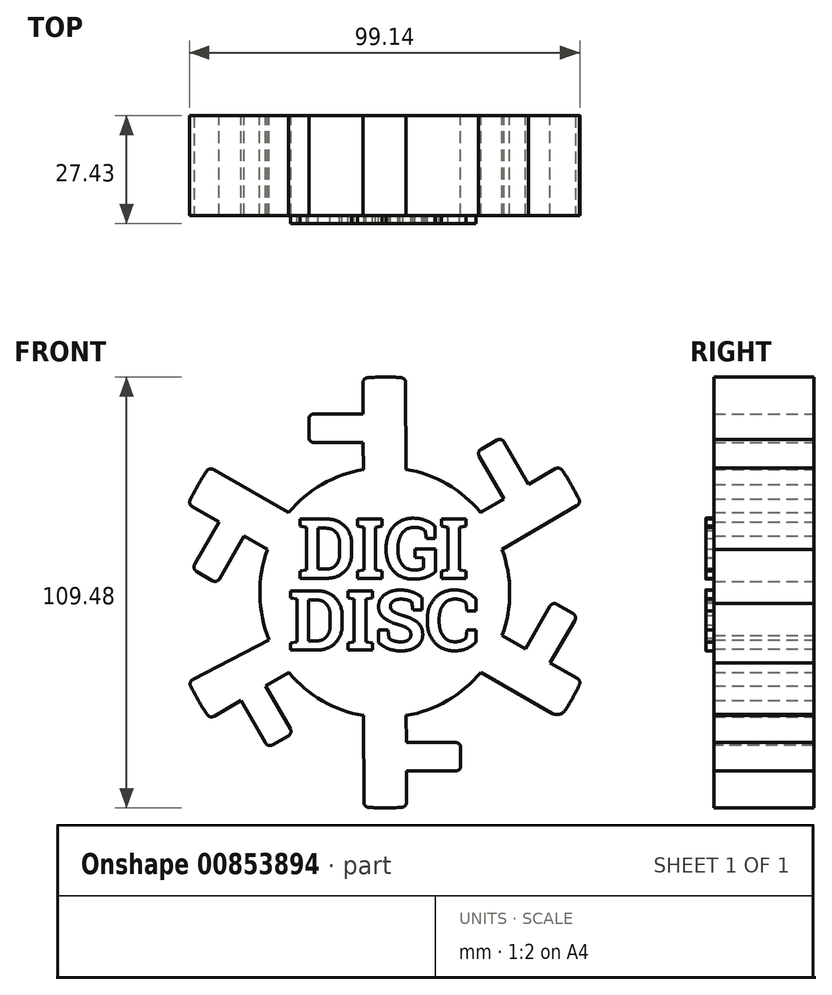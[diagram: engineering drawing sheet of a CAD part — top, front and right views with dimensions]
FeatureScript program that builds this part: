
annotation { "Feature Type Name" : "Feature", "Feature Type Description" : "" }
export const myFeature = defineFeature(function(context is Context, id is Id, definition is map)
    precondition{}
    {
        {
            var Q0;
            Q0=qCreatedBy(makeId("Front.planeOp"),FACE);
            var sketch = newSketch(context, id + "F0", { "sketchPlane" : qUnion([Q0])});
            skArc(sketch, "E0", {"start": v(5.31, 54.48) * mm, "mid": v(-0.12, 54.74) * mm, "end": v(-5.54, 54.46) * mm});
            skCircle(sketch, "E1", {"center": v(0, 0) * mm, "radius": 31.75 * mm});
            skLineSegment(sketch, "E2.left", {"start": v(-5.45, 31.28) * mm, "end": v(-5.48, 38.1) * mm});
            skLineSegment(sketch, "E2.right", {"start": v(5.4, 31.29) * mm, "end": v(5.31, 54.48) * mm});
            skLineSegment(sketch, "E3.bottom", {"start": v(-5.48, 38.1) * mm, "end": v(-19.28, 38.1) * mm});
            skLineSegment(sketch, "E3.top", {"start": v(-5.5, 45.36) * mm, "end": v(-19.28, 45.36) * mm});
            skLineSegment(sketch, "E3.left", {"start": v(5.38, 38.1) * mm, "end": v(5.38, 45.36) * mm});
            skLineSegment(sketch, "E3.right", {"start": v(-19.28, 38.1) * mm, "end": v(-19.28, 45.36) * mm});
            skLineSegment(sketch, "E4.trimOffspring", {"start": v(-5.5, 45.36) * mm, "end": v(-5.54, 54.46) * mm});
            skLineSegment(sketch, "E5.1.0", {"start": v(-30.3, 23.7) * mm, "end": v(-36.6, 27.34) * mm});
            skLineSegment(sketch, "E5.1.1", {"start": v(-24.4, 20.32) * mm, "end": v(-44.53, 31.84) * mm});
            skArc(sketch, "E5.1.2", {"start": v(-44.53, 31.84) * mm, "mid": v(-47.47, 27.27) * mm, "end": v(-49.94, 22.43) * mm});
            skLineSegment(sketch, "E5.1.3", {"start": v(-42.04, 17.9) * mm, "end": v(-49.94, 22.43) * mm});
            skLineSegment(sketch, "E5.1.4", {"start": v(-29.81, 10.92) * mm, "end": v(-35.74, 14.3) * mm});
            skLineSegment(sketch, "E5.1.5", {"start": v(-35.74, 14.3) * mm, "end": v(-42.64, 2.35) * mm});
            skLineSegment(sketch, "E5.1.6", {"start": v(-42.64, 2.35) * mm, "end": v(-48.92, 5.98) * mm});
            skLineSegment(sketch, "E5.1.7", {"start": v(-42.04, 17.9) * mm, "end": v(-48.92, 5.98) * mm});
            skArc(sketch, "E5.2.2", {"start": v(-49.84, -22.64) * mm, "mid": v(-47.35, -27.47) * mm, "end": v(-44.4, -32.03) * mm});
            skLineSegment(sketch, "E5.2.3", {"start": v(-36.53, -27.45) * mm, "end": v(-44.4, -32.03) * mm});
            skLineSegment(sketch, "E5.2.4", {"start": v(-24.36, -20.36) * mm, "end": v(-30.26, -23.8) * mm});
            skLineSegment(sketch, "E5.2.5", {"start": v(-30.26, -23.8) * mm, "end": v(-23.35, -35.75) * mm});
            skLineSegment(sketch, "E5.2.6", {"start": v(-23.35, -35.75) * mm, "end": v(-29.64, -39.38) * mm});
            skLineSegment(sketch, "E5.2.7", {"start": v(-36.53, -27.45) * mm, "end": v(-29.64, -39.38) * mm});
            skLineSegment(sketch, "E5.3.1", {"start": v(-5.4, -31.29) * mm, "end": v(-5.31, -54.48) * mm});
            skArc(sketch, "E5.3.2", {"start": v(-5.31, -54.48) * mm, "mid": v(0.12, -54.74) * mm, "end": v(5.54, -54.46) * mm});
            skLineSegment(sketch, "E5.3.3", {"start": v(5.5, -45.36) * mm, "end": v(5.54, -54.46) * mm});
            skLineSegment(sketch, "E5.3.4", {"start": v(5.45, -31.28) * mm, "end": v(5.48, -38.1) * mm});
            skLineSegment(sketch, "E5.3.5", {"start": v(5.48, -38.1) * mm, "end": v(19.28, -38.1) * mm});
            skLineSegment(sketch, "E5.3.6", {"start": v(19.28, -38.1) * mm, "end": v(19.28, -45.36) * mm});
            skLineSegment(sketch, "E5.3.7", {"start": v(5.5, -45.36) * mm, "end": v(19.28, -45.36) * mm});
            skLineSegment(sketch, "E5.4.0", {"start": v(30.3, -23.7) * mm, "end": v(36.6, -27.34) * mm});
            skLineSegment(sketch, "E5.4.1", {"start": v(24.4, -20.32) * mm, "end": v(44.53, -31.84) * mm});
            skArc(sketch, "E5.4.2", {"start": v(44.53, -31.84) * mm, "mid": v(47.47, -27.27) * mm, "end": v(49.94, -22.43) * mm});
            skLineSegment(sketch, "E5.4.3", {"start": v(42.04, -17.9) * mm, "end": v(49.94, -22.43) * mm});
            skLineSegment(sketch, "E5.4.4", {"start": v(29.81, -10.92) * mm, "end": v(35.74, -14.3) * mm});
            skLineSegment(sketch, "E5.4.5", {"start": v(35.74, -14.3) * mm, "end": v(42.64, -2.35) * mm});
            skLineSegment(sketch, "E5.4.6", {"start": v(42.64, -2.35) * mm, "end": v(48.92, -5.98) * mm});
            skLineSegment(sketch, "E5.4.7", {"start": v(42.04, -17.9) * mm, "end": v(48.92, -5.98) * mm});
            skLineSegment(sketch, "E6.3.5.0", {"start": v(29.8, 10.96) * mm, "end": v(49.84, 22.64) * mm});
            skArc(sketch, "E6.6.5.0", {"start": v(49.84, 22.64) * mm, "mid": v(47.35, 27.47) * mm, "end": v(44.4, 32.03) * mm});
            skLineSegment(sketch, "E6.10.5.0", {"start": v(36.53, 27.45) * mm, "end": v(44.4, 32.03) * mm});
            skLineSegment(sketch, "E6.13.5.0", {"start": v(24.36, 20.36) * mm, "end": v(30.26, 23.8) * mm});
            skLineSegment(sketch, "E6.16.5.0", {"start": v(30.26, 23.8) * mm, "end": v(23.35, 35.75) * mm});
            skLineSegment(sketch, "E6.19.5.0", {"start": v(23.35, 35.75) * mm, "end": v(29.64, 39.38) * mm});
            skLineSegment(sketch, "E6.22.5.0", {"start": v(36.53, 27.45) * mm, "end": v(29.64, 39.38) * mm});
            skLineSegment(sketch, "E7", {"start": v(-49.84, -22.64) * mm, "end": v(-29.37, -12.07) * mm});
            skSolve(sketch);
        }
        {
            var Q0;
            {var subQ0=sQuery(id+"F0.wireOp",EDGE,"E1");var subQ5=makeQuery(id+"F0.imprint","INTERSECT",VERTEX,{"derivedFrom":[subQ0,sQuery(id+"F0.wireOp",EDGE,"E5.4.1")]});Q0=makeQuery(id+"F0.imprint","IMPRINT",FACE,{"disambiguationData":[TD([[makeQuery(id+"F0.imprint","IMPRINT",EDGE,{"disambiguationData":[TD([[subQ5,-1.0]])],"derivedFrom":subQ0}),1.0]])]});}
            var Q1;
            {var subQ0=sQuery(id+"F0.wireOp",EDGE,"E5.1.2");Q1=makeQuery(id+"F0.imprint","IMPRINT",FACE,{"disambiguationData":[TD([[makeQuery(id+"F0.imprint","IMPRINT",EDGE,{"derivedFrom":subQ0}),1.0]])]});}
            var Q2;
            {var subQ5=sQuery(id+"F0.wireOp",EDGE,"E0");Q2=makeQuery(id+"F0.imprint","IMPRINT",FACE,{"disambiguationData":[TD([[makeQuery(id+"F0.imprint","IMPRINT",EDGE,{"derivedFrom":subQ5}),1.0]])]});}
            var Q3;
            {var subQ0=sQuery(id+"F0.wireOp",EDGE,"E5.4.2");Q3=makeQuery(id+"F0.imprint","IMPRINT",FACE,{"disambiguationData":[TD([[makeQuery(id+"F0.imprint","IMPRINT",EDGE,{"derivedFrom":subQ0}),1.0]])]});}
            var Q4;
            {var subQ0=sQuery(id+"F0.wireOp",EDGE,"E5.3.2");Q4=makeQuery(id+"F0.imprint","IMPRINT",FACE,{"disambiguationData":[TD([[makeQuery(id+"F0.imprint","IMPRINT",EDGE,{"derivedFrom":subQ0}),1.0]])]});}
            var Q5;
            {var subQ0=sQuery(id+"F0.wireOp",EDGE,"E5.2.2");Q5=makeQuery(id+"F0.imprint","IMPRINT",FACE,{"disambiguationData":[TD([[makeQuery(id+"F0.imprint","IMPRINT",EDGE,{"derivedFrom":subQ0}),1.0]])]});}
            var Q6;
            {var subQ0=sQuery(id+"F0.wireOp",EDGE,"E6.6.5.0");Q6=makeQuery(id+"F0.imprint","IMPRINT",FACE,{"disambiguationData":[TD([[makeQuery(id+"F0.imprint","IMPRINT",EDGE,{"derivedFrom":subQ0}),1.0]])]});}
            extrude(context, id + "F1", {"entities" : qUnion([Q0, Q1, Q2, Q3, Q4, Q5, Q6]), "depth" : 25.4 * mm, "offsetDistance" : 25.4 * mm});
        }
        {
            var Q0;
            Q0=makeQuery(id+"F1.opExtrude","SWEPT_EDGE",EDGE,{"disambiguationData":[OSD([sQuery(id+"F0.wireOp",EDGE,"E0"),sQuery(id+"F0.wireOp",EDGE,"E2.right")])]});
            var Q1;
            Q1=makeQuery(id+"F1.opExtrude","SWEPT_EDGE",EDGE,{"disambiguationData":[OSD([sQuery(id+"F0.wireOp",EDGE,"E0"),sQuery(id+"F0.wireOp",EDGE,"E4.trimOffspring")])]});
            fillet(context, id + "F2", {"entities" : qUnion([Q0, Q1]), "radius" : 1.27 * mm, "tangentPropagation" : true, "allowEdgeOverflow" : false});
        }
        {
            var Q0;
            Q0=makeQuery(id+"F1.opExtrude","SWEPT_EDGE",EDGE,{"disambiguationData":[OSD([sQuery(id+"F0.wireOp",EDGE,"E3.top"),sQuery(id+"F0.wireOp",EDGE,"E3.right")])]});
            var Q1;
            Q1=makeQuery(id+"F1.opExtrude","SWEPT_EDGE",EDGE,{"disambiguationData":[OSD([sQuery(id+"F0.wireOp",EDGE,"E3.bottom"),sQuery(id+"F0.wireOp",EDGE,"E3.right")])]});
            fillet(context, id + "F3", {"entities" : qUnion([Q0, Q1]), "radius" : 1.27 * mm, "tangentPropagation" : true, "allowEdgeOverflow" : false});
        }
        {
            var Q0;
            Q0=makeQuery(id+"F1.opExtrude","SWEPT_EDGE",EDGE,{"disambiguationData":[OSD([sQuery(id+"F0.wireOp",EDGE,"E6.19.5.0"),sQuery(id+"F0.wireOp",EDGE,"E6.22.5.0")])]});
            var Q1;
            Q1=makeQuery(id+"F1.opExtrude","SWEPT_EDGE",EDGE,{"disambiguationData":[OSD([sQuery(id+"F0.wireOp",EDGE,"E6.16.5.0"),sQuery(id+"F0.wireOp",EDGE,"E6.19.5.0")])]});
            var Q2;
            Q2=makeQuery(id+"F1.opExtrude","SWEPT_EDGE",EDGE,{"disambiguationData":[OSD([sQuery(id+"F0.wireOp",EDGE,"E6.6.5.0"),sQuery(id+"F0.wireOp",EDGE,"E6.10.5.0")])]});
            var Q3;
            Q3=makeQuery(id+"F1.opExtrude","SWEPT_EDGE",EDGE,{"disambiguationData":[OSD([sQuery(id+"F0.wireOp",EDGE,"E6.3.5.0"),sQuery(id+"F0.wireOp",EDGE,"E6.6.5.0")])]});
            var Q4;
            Q4=makeQuery(id+"F1.opExtrude","SWEPT_EDGE",EDGE,{"disambiguationData":[OSD([sQuery(id+"F0.wireOp",EDGE,"E5.4.6"),sQuery(id+"F0.wireOp",EDGE,"E5.4.7")])]});
            var Q5;
            Q5=makeQuery(id+"F1.opExtrude","SWEPT_EDGE",EDGE,{"disambiguationData":[OSD([sQuery(id+"F0.wireOp",EDGE,"E5.4.2"),sQuery(id+"F0.wireOp",EDGE,"E5.4.3")])]});
            var Q6;
            Q6=makeQuery(id+"F1.opExtrude","SWEPT_EDGE",EDGE,{"disambiguationData":[OSD([sQuery(id+"F0.wireOp",EDGE,"E5.4.5"),sQuery(id+"F0.wireOp",EDGE,"E5.4.6")])]});
            var Q7;
            Q7=makeQuery(id+"F1.opExtrude","SWEPT_EDGE",EDGE,{"disambiguationData":[OSD([sQuery(id+"F0.wireOp",EDGE,"E5.3.6"),sQuery(id+"F0.wireOp",EDGE,"E5.3.7")])]});
            var Q8;
            Q8=makeQuery(id+"F1.opExtrude","SWEPT_EDGE",EDGE,{"disambiguationData":[OSD([sQuery(id+"F0.wireOp",EDGE,"E5.3.5"),sQuery(id+"F0.wireOp",EDGE,"E5.3.6")])]});
            var Q9;
            Q9=makeQuery(id+"F1.opExtrude","SWEPT_EDGE",EDGE,{"disambiguationData":[OSD([sQuery(id+"F0.wireOp",EDGE,"E5.3.2"),sQuery(id+"F0.wireOp",EDGE,"E5.3.3")])]});
            var Q10;
            Q10=makeQuery(id+"F1.opExtrude","SWEPT_EDGE",EDGE,{"disambiguationData":[OSD([sQuery(id+"F0.wireOp",EDGE,"E5.3.1"),sQuery(id+"F0.wireOp",EDGE,"E5.3.2")])]});
            var Q11;
            Q11=makeQuery(id+"F1.opExtrude","SWEPT_EDGE",EDGE,{"disambiguationData":[OSD([sQuery(id+"F0.wireOp",EDGE,"E5.2.6"),sQuery(id+"F0.wireOp",EDGE,"E5.2.7")])]});
            var Q12;
            Q12=makeQuery(id+"F1.opExtrude","SWEPT_EDGE",EDGE,{"disambiguationData":[OSD([sQuery(id+"F0.wireOp",EDGE,"E5.2.5"),sQuery(id+"F0.wireOp",EDGE,"E5.2.6")])]});
            var Q13;
            Q13=makeQuery(id+"F1.opExtrude","SWEPT_EDGE",EDGE,{"disambiguationData":[OSD([sQuery(id+"F0.wireOp",EDGE,"E5.2.2"),sQuery(id+"F0.wireOp",EDGE,"E5.2.3")])]});
            var Q14;
            Q14=makeQuery(id+"F1.opExtrude","SWEPT_EDGE",EDGE,{"disambiguationData":[OSD([sQuery(id+"F0.wireOp",EDGE,"E5.2.1"),sQuery(id+"F0.wireOp",EDGE,"E5.2.2")])]});
            var Q15;
            Q15=makeQuery(id+"F1.opExtrude","SWEPT_EDGE",EDGE,{"disambiguationData":[OSD([sQuery(id+"F0.wireOp",EDGE,"E5.1.6"),sQuery(id+"F0.wireOp",EDGE,"E5.1.7")])]});
            var Q16;
            Q16=makeQuery(id+"F1.opExtrude","SWEPT_EDGE",EDGE,{"disambiguationData":[OSD([sQuery(id+"F0.wireOp",EDGE,"E5.1.5"),sQuery(id+"F0.wireOp",EDGE,"E5.1.6")])]});
            var Q17;
            Q17=makeQuery(id+"F1.opExtrude","SWEPT_EDGE",EDGE,{"disambiguationData":[OSD([sQuery(id+"F0.wireOp",EDGE,"E5.1.2"),sQuery(id+"F0.wireOp",EDGE,"E5.1.3")])]});
            var Q18;
            Q18=makeQuery(id+"F1.opExtrude","SWEPT_EDGE",EDGE,{"disambiguationData":[OSD([sQuery(id+"F0.wireOp",EDGE,"E5.1.1"),sQuery(id+"F0.wireOp",EDGE,"E5.1.2")])]});
            fillet(context, id + "F4", {"entities" : qUnion([Q0, Q1, Q2, Q3, Q4, Q5, Q6, Q7, Q8, Q9, Q10, Q11, Q12, Q13, Q14, Q15, Q16, Q17, Q18]), "radius" : 1.27 * mm, "tangentPropagation" : true, "allowEdgeOverflow" : false});
        }
        {
            var Q0;
            Q0=makeQuery(id+"F1.opExtrude","SWEPT_EDGE",EDGE,{"disambiguationData":[OSD([sQuery(id+"F0.wireOp",EDGE,"E5.4.1"),sQuery(id+"F0.wireOp",EDGE,"E5.4.2")])]});
            fillet(context, id + "F5", {"entities" : qUnion([Q0]), "radius" : 2.54 * mm, "tangentPropagation" : true, "allowEdgeOverflow" : false});
        }
        {
            var Q0;
            Q0=makeQuery(id+"F1.opExtrude","CAP_FACE",FACE,{"disambiguationData":[OSD([sQuery(id+"F0.wireOp",EDGE,"E0"),sQuery(id+"F0.wireOp",EDGE,"E1"),sQuery(id+"F0.wireOp",EDGE,"E2.left"),sQuery(id+"F0.wireOp",EDGE,"E2.right"),sQuery(id+"F0.wireOp",EDGE,"E3.bottom"),sQuery(id+"F0.wireOp",EDGE,"E3.top"),sQuery(id+"F0.wireOp",EDGE,"E3.right"),sQuery(id+"F0.wireOp",EDGE,"E4.trimOffspring"),sQuery(id+"F0.wireOp",EDGE,"E5.1.1"),sQuery(id+"F0.wireOp",EDGE,"E5.1.2"),sQuery(id+"F0.wireOp",EDGE,"E5.1.3"),sQuery(id+"F0.wireOp",EDGE,"E5.1.4"),sQuery(id+"F0.wireOp",EDGE,"E5.1.5"),sQuery(id+"F0.wireOp",EDGE,"E5.1.6"),sQuery(id+"F0.wireOp",EDGE,"E5.1.7"),sQuery(id+"F0.wireOp",EDGE,"E5.2.2"),sQuery(id+"F0.wireOp",EDGE,"E5.2.3"),sQuery(id+"F0.wireOp",EDGE,"E5.2.4"),sQuery(id+"F0.wireOp",EDGE,"E5.2.5"),sQuery(id+"F0.wireOp",EDGE,"E5.2.6"),sQuery(id+"F0.wireOp",EDGE,"E5.2.7"),sQuery(id+"F0.wireOp",EDGE,"E5.3.1"),sQuery(id+"F0.wireOp",EDGE,"E5.3.2"),sQuery(id+"F0.wireOp",EDGE,"E5.3.3"),sQuery(id+"F0.wireOp",EDGE,"E5.3.4"),sQuery(id+"F0.wireOp",EDGE,"E5.3.5"),sQuery(id+"F0.wireOp",EDGE,"E5.3.6"),sQuery(id+"F0.wireOp",EDGE,"E5.3.7"),sQuery(id+"F0.wireOp",EDGE,"E5.4.1"),sQuery(id+"F0.wireOp",EDGE,"E5.4.2"),sQuery(id+"F0.wireOp",EDGE,"E5.4.3"),sQuery(id+"F0.wireOp",EDGE,"E5.4.4"),sQuery(id+"F0.wireOp",EDGE,"E5.4.5"),sQuery(id+"F0.wireOp",EDGE,"E5.4.6"),sQuery(id+"F0.wireOp",EDGE,"E5.4.7"),sQuery(id+"F0.wireOp",EDGE,"E6.3.5.0"),sQuery(id+"F0.wireOp",EDGE,"E6.6.5.0"),sQuery(id+"F0.wireOp",EDGE,"E6.10.5.0"),sQuery(id+"F0.wireOp",EDGE,"E6.13.5.0"),sQuery(id+"F0.wireOp",EDGE,"E6.16.5.0"),sQuery(id+"F0.wireOp",EDGE,"E6.19.5.0"),sQuery(id+"F0.wireOp",EDGE,"E6.22.5.0"),sQuery(id+"F0.wireOp",EDGE,"E7")])],"isStart":false});
            var sketch = newSketch(context, id + "F6", { "sketchPlane" : qUnion([Q0])});
            skText(sketch, "E8", { "text": "DIGI", "fontName": "RobotoSlab-Bold.ttf"});
            skText(sketch, "E9", { "text": "DISC", "fontName": "RobotoSlab-Bold.ttf"});
            const initialGuessF6  = {"E8": [-0.02209, 0.00361, 1, 0, 0.01524], "E9": [-0.02452, -0.01462, 1, 0, 0.01524]};
            skSetInitialGuess(sketch, initialGuessF6);
            skSolve(sketch);
        }
        {
            var Q0;
            Q0=qSketchRegion(id+"F6",true);
            extrude(context, id + "F7", {"entities" : qUnion([Q0]), "operationType" : NewBodyOperationType.ADD, "depth" : 2.03 * mm, "offsetDistance" : 25.4 * mm});
        }
    });
